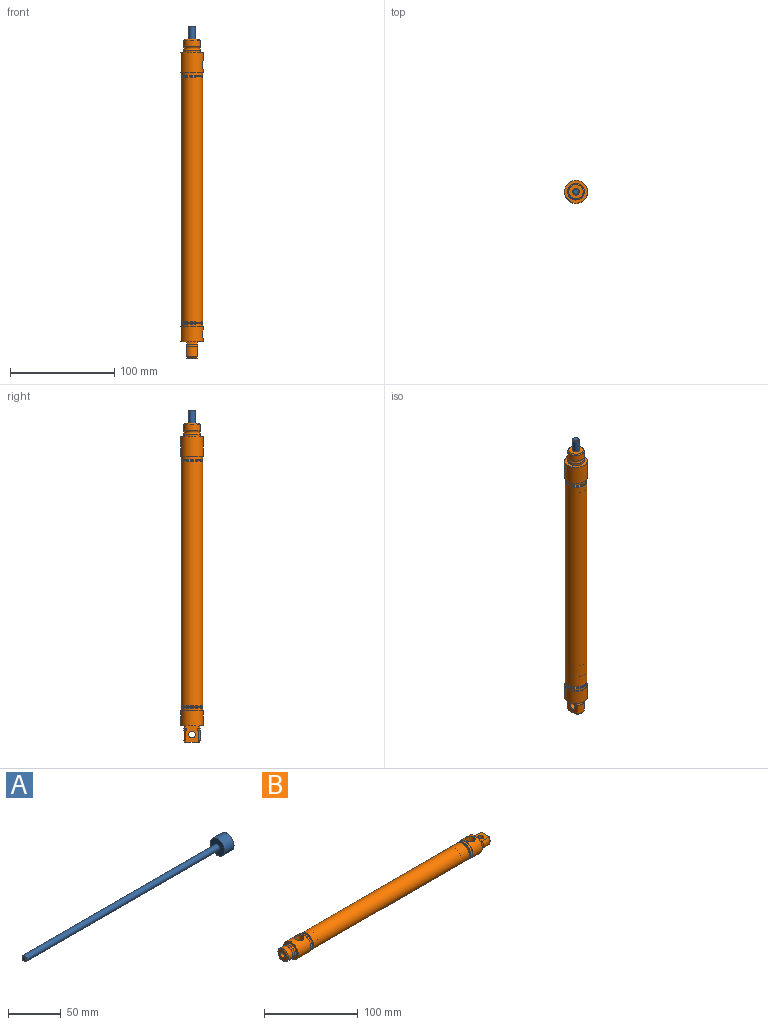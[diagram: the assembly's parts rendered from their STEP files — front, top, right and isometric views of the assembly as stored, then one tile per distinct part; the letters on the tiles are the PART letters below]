
ASSEMBLY  parts=2 mates=1
PART A: 6 faces, bbox 271.9x19.1x19.1 mm
  f0: cone r=2.67mm half-angle=45deg, axis (1,0,0), area 13.2mm2, adj f2,f3
  f1: cylinder r=9.53mm len=19.05mm, axis (1,0,0), area 760.1mm2, adj f4,f5
  f2: cylinder r=3.17mm len=258.7mm, axis (1,0,0), area 5160.8mm2, adj f0,f4
  f3: plane 5.33x5.33mm, normal (-1,0,0), area 22.3mm2, adj f0
  f4: plane 19.05x19.05mm, normal (-1,0,0), area 253.4mm2, adj f1,f2
  f5: plane 19.05x19.05mm, normal (1,0,0), area 285mm2, adj f1
PART B: 50 faces, bbox 305.8x22.1x22.1 mm
  f0: torus R=8.49mm, axis (-1,0,0), area 29.4mm2, adj f1,f47,f48,f49
  f1: plane 15.97x12.83mm, normal (0,0,-1), area 162.4mm2, adj f0,f2,f3,f4,f5,f43,f44,f45
  f2: cylinder r=3.17mm len=9.65mm, axis (0,0,1), area 192.5mm2, adj f1,f48
  f3: torus R=8.49mm, axis (-1,0,0), area 29.4mm2, adj f1,f4,f46,f48
  f4: cylinder r=7.94mm len=9.65mm, axis (-1,0,0), area 25mm2, adj f1,f3,f5,f48
  f5: plane 21.84x21.84mm, normal (1,0,0), area 231.6mm2, adj f1,f4,f6,f48,f49
  f6: cylinder r=10.92mm len=21.84mm, axis (-1,0,0), area 891mm2, adj f5,f7,f11
  f7: cone r=5.14mm half-angle=1.7deg, axis (0,0,1), area 219.4mm2, adj f6,f8
  f8: plane 9.87x9.87mm, normal (0,0,1), area 20.7mm2, adj f7,f9
  f9: cylinder r=4.22mm len=8.43mm, axis (0,0,1), area 124.5mm2, adj f8,f10
  f10: cone r=4.22mm half-angle=59deg, axis (0,0,1), area 65.2mm2, adj f9
  f11: plane 21.84x21.84mm, normal (-1,0,0), area 42.3mm2, adj f6,f12
  f12: cylinder r=10.29mm len=20.57mm, axis (-1,0,0), area 164.2mm2, adj f11,f13
  f13: plane 20.57x20.57mm, normal (-1,0,0), area 47.4mm2, adj f12,f14
  f14: cone r=10.29mm half-angle=45deg, axis (-1,0,0), area 67.1mm2, adj f13,f15
  f15: cylinder r=10.29mm len=20.57mm, axis (-1,0,0), area 32.8mm2, adj f14,f16
  f16: plane 20.57x20.57mm, normal (-1,0,0), area 47.4mm2, adj f15,f17
  f17: cone r=10.29mm half-angle=45deg, axis (-1,0,0), area 67.1mm2, adj f16,f18
  f18: cylinder r=10.29mm len=234.57mm, axis (-1,0,0), area 15161.4mm2, adj f17,f19
  f19: cone r=9.4mm half-angle=45deg, axis (1,0,0), area 77.8mm2, adj f18,f20
  f20: plane 20.57x20.57mm, normal (1,0,0), area 55mm2, adj f19,f21
  f21: cylinder r=10.29mm len=20.57mm, axis (-1,0,0), area 24.6mm2, adj f20,f22
  f22: cone r=9.4mm half-angle=45deg, axis (1,0,0), area 77.8mm2, adj f21,f23
  f23: plane 20.57x20.57mm, normal (1,0,0), area 55mm2, adj f22,f24
  f24: cylinder r=10.29mm len=20.57mm, axis (-1,0,0), area 164.2mm2, adj f23,f25
  f25: plane 21.84x21.84mm, normal (1,0,0), area 42.3mm2, adj f24,f26
  f26: cylinder r=10.92mm len=21.84mm, axis (-1,0,0), area 1222.2mm2, adj f25,f27,f42
  f27: cone r=5.14mm half-angle=1.7deg, axis (0,0,1), area 219.4mm2, adj f26,f28
  f28: plane 9.87x9.87mm, normal (0,0,1), area 20.7mm2, adj f27,f29
  f29: cylinder r=4.22mm len=8.43mm, axis (0,0,1), area 79.9mm2, adj f28,f30,f31,f32
  f30: cone r=4.22mm half-angle=59deg, axis (0,0,1), area 0mm2, adj f29,f32
  f31: cone r=4.22mm half-angle=59deg, axis (0,0,1), area 0mm2, adj f29,f32
  f32: cylinder r=3.17mm len=43.31mm, axis (1,0,0), area 778.9mm2, adj f29,f30,f31,f33,f38,f39
  f33: plane 13.84x13.84mm, normal (-1,0,0), area 118.8mm2, adj f32,f34
  f34: cone r=6.92mm half-angle=45deg, axis (1,0,0), area 67.1mm2, adj f33,f35
  f35: cylinder r=7.94mm len=15.88mm, axis (-1,0,0), area 316.7mm2, adj f34,f36
  f36: torus R=9.28mm, axis (-1,0,0), area 162.1mm2, adj f35,f37
  f37: cylinder r=7.94mm len=15.88mm, axis (-1,0,0), area 114mm2, adj f36,f42
  f38: cone r=4.22mm half-angle=59deg, axis (0,0,1), area 0mm2, adj f32
  f39: plane 19.05x19.05mm, normal (1,0,0), area 253.4mm2, adj f32,f40
  f40: cylinder r=9.53mm len=215.9mm, axis (1,0,0), area 12921mm2, adj f39,f41
  f41: plane 19.05x19.05mm, normal (-1,0,0), area 285mm2, adj f40
  f42: plane 21.84x21.84mm, normal (-1,0,0), area 176.8mm2, adj f26,f37
  f43: cone r=7.94mm half-angle=45deg, axis (-1,0,0), area 15.2mm2, adj f1,f44,f47,f48
  f44: plane 13.84x9.65mm, normal (1,0,0), area 121.8mm2, adj f1,f43,f45,f48
  f45: cone r=7.94mm half-angle=45deg, axis (-1,0,0), area 15.2mm2, adj f1,f44,f46,f48
  f46: cylinder r=7.94mm len=10.03mm, axis (-1,0,0), area 104.1mm2, adj f1,f3,f45,f48
  f47: cylinder r=7.94mm len=10.03mm, axis (-1,0,0), area 104.1mm2, adj f0,f1,f43,f48
  f48: plane 15.97x12.83mm, normal (0,0,1), area 162.4mm2, adj f0,f2,f3,f4,f5,f43,f44,f45
  f49: cylinder r=7.94mm len=9.65mm, axis (-1,0,0), area 25mm2, adj f0,f1,f5,f48
PLACE A rot(axis=(0.58,0.58,-0.58),120deg) t=(0,0,368.57)mm
PLACE B rot(axis=(0,1,0),90deg) t=(0,0,0)mm fixed
MATE slider A.f0 <-> B.f0  axis (0,0,1) through (0,0,12.7)mm
